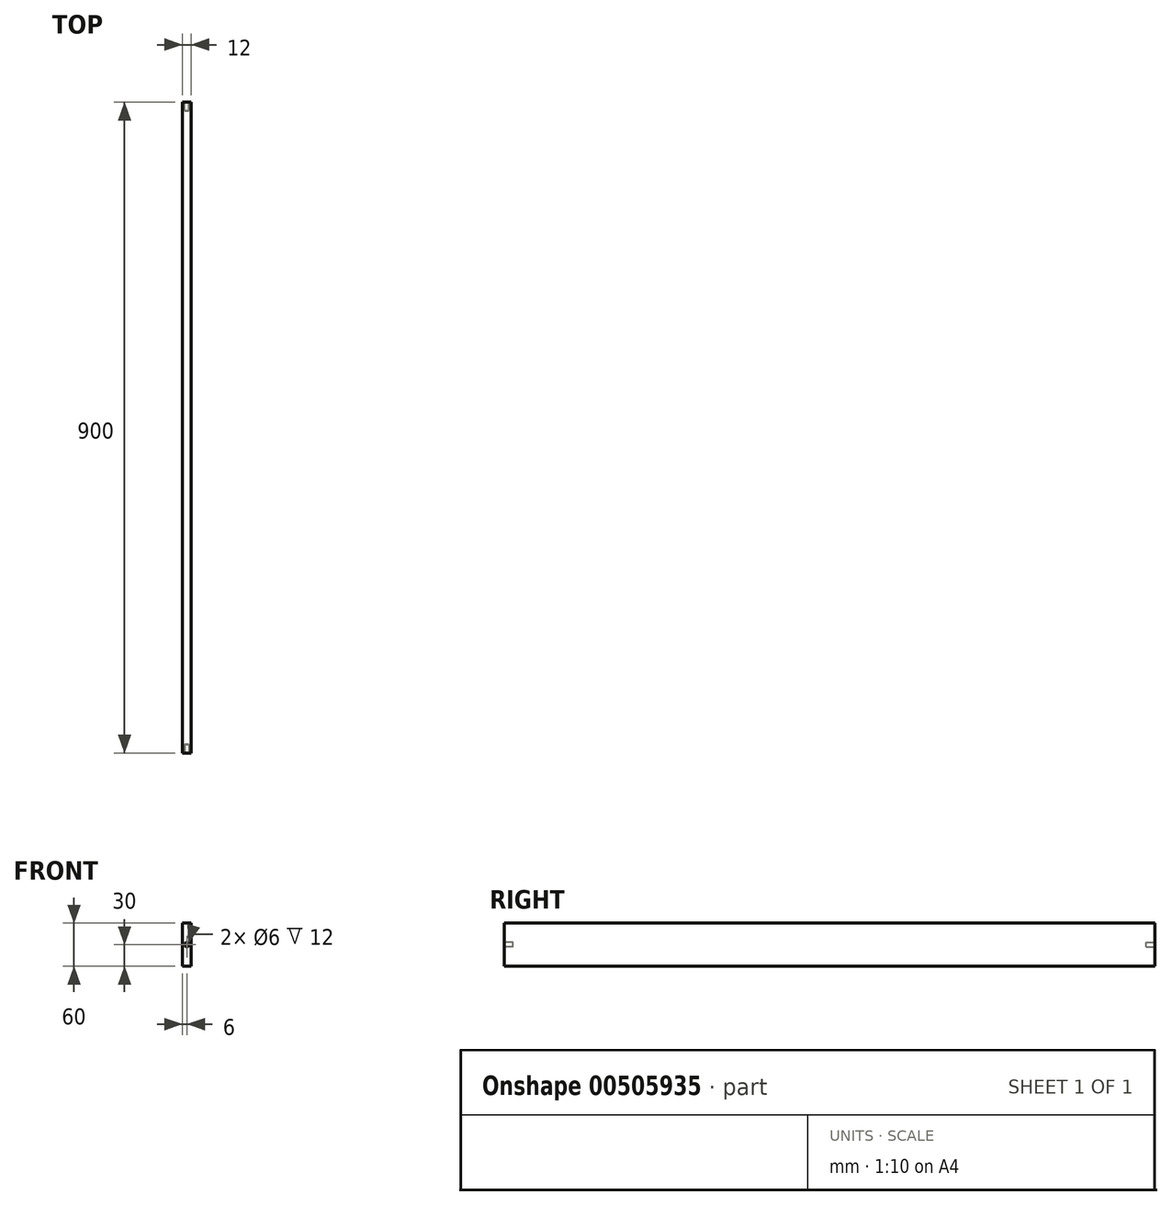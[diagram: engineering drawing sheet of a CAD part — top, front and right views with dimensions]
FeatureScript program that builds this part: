
annotation { "Feature Type Name" : "Feature", "Feature Type Description" : "" }
export const myFeature = defineFeature(function(context is Context, id is Id, definition is map)
    precondition{}
    {
        {
            var Q0;
            Q0=qCreatedBy(makeId("Front.planeOp"),FACE);
            var sketch = newSketch(context, id + "F0", { "sketchPlane" : qUnion([Q0])});
            skLineSegment(sketch, "E0.bottom", {"start": v(0, 0) * mm, "end": v(12, 0) * mm});
            skLineSegment(sketch, "E0.top", {"start": v(0, 60) * mm, "end": v(12, 60) * mm});
            skLineSegment(sketch, "E0.left", {"start": v(0, 0) * mm, "end": v(0, 60) * mm});
            skLineSegment(sketch, "E0.right", {"start": v(12, 0) * mm, "end": v(12, 60) * mm});
            skSolve(sketch);
        }
        {
            var Q0;
            Q0=makeQuery(id+"F0.imprint","IMPRINT",FACE,{"disambiguationData":[TD([[makeQuery(id+"F0.imprint","IMPRINT",EDGE,{"derivedFrom":sQuery(id+"F0.wireOp",EDGE,"E0.bottom")}),1.0]])]});
            extrude(context, id + "F1", {"entities" : qUnion([Q0]), "depth" : 900 * mm, "offsetDistance" : 25 * mm});
        }
        {
            var Q0;
            Q0=makeQuery(id+"F1.opExtrude","CAP_FACE",FACE,{"disambiguationData":[OSD([sQuery(id+"F0.wireOp",EDGE,"E0.bottom"),sQuery(id+"F0.wireOp",EDGE,"E0.top"),sQuery(id+"F0.wireOp",EDGE,"E0.left"),sQuery(id+"F0.wireOp",EDGE,"E0.right")])],"isStart":false});
            var sketch = newSketch(context, id + "F2", { "sketchPlane" : qUnion([Q0])});
            skCircle(sketch, "E1", {"center": v(6, 30) * mm, "radius": 3 * mm});
            skPoint(sketch, "E1.centerSnap0", {"position": v(12, 30) * mm});
            skPoint(sketch, "E1.centerSnap1", {"position": v(6, 60) * mm});
            skSolve(sketch);
        }
        {
            var Q0;
            Q0=qCreatedBy(makeId("Front.planeOp"),FACE);
            var sketch = newSketch(context, id + "F3", { "sketchPlane" : qUnion([Q0])});
            skCircle(sketch, "E2.0", {"center": v(6, 30) * mm, "radius": 3 * mm});
            skSolve(sketch);
        }
        {
            var Q0;
            Q0=makeQuery(id+"F3.imprint","IMPRINT",FACE,{"disambiguationData":[TD([[makeQuery(id+"F3.imprint","IMPRINT",EDGE,{"derivedFrom":sQuery(id+"F3.wireOp",EDGE,"E2.0")}),1.0]])]});
            var Q1;
            Q1=sQuery(id+"F3.wireOp",EDGE,"E2.0");
            extrude(context, id + "F4", {"entities" : qUnion([Q0]), "operationType" : NewBodyOperationType.REMOVE, "surfaceEntities" : qUnion([Q1]), "depth" : 12 * mm, "offsetDistance" : 25 * mm});
        }
        {
            var Q0;
            Q0=makeQuery(id+"F2.imprint","IMPRINT",FACE,{"disambiguationData":[TD([[makeQuery(id+"F2.imprint","IMPRINT",EDGE,{"derivedFrom":sQuery(id+"F2.wireOp",EDGE,"E1")}),1.0]])]});
            var Q1;
            Q1=sQuery(id+"F2.wireOp",EDGE,"E1");
            extrude(context, id + "F5", {"entities" : qUnion([Q0]), "operationType" : NewBodyOperationType.REMOVE, "surfaceEntities" : qUnion([Q1]), "oppositeDirection" : true, "depth" : 12 * mm, "offsetDistance" : 25 * mm});
        }
    });
